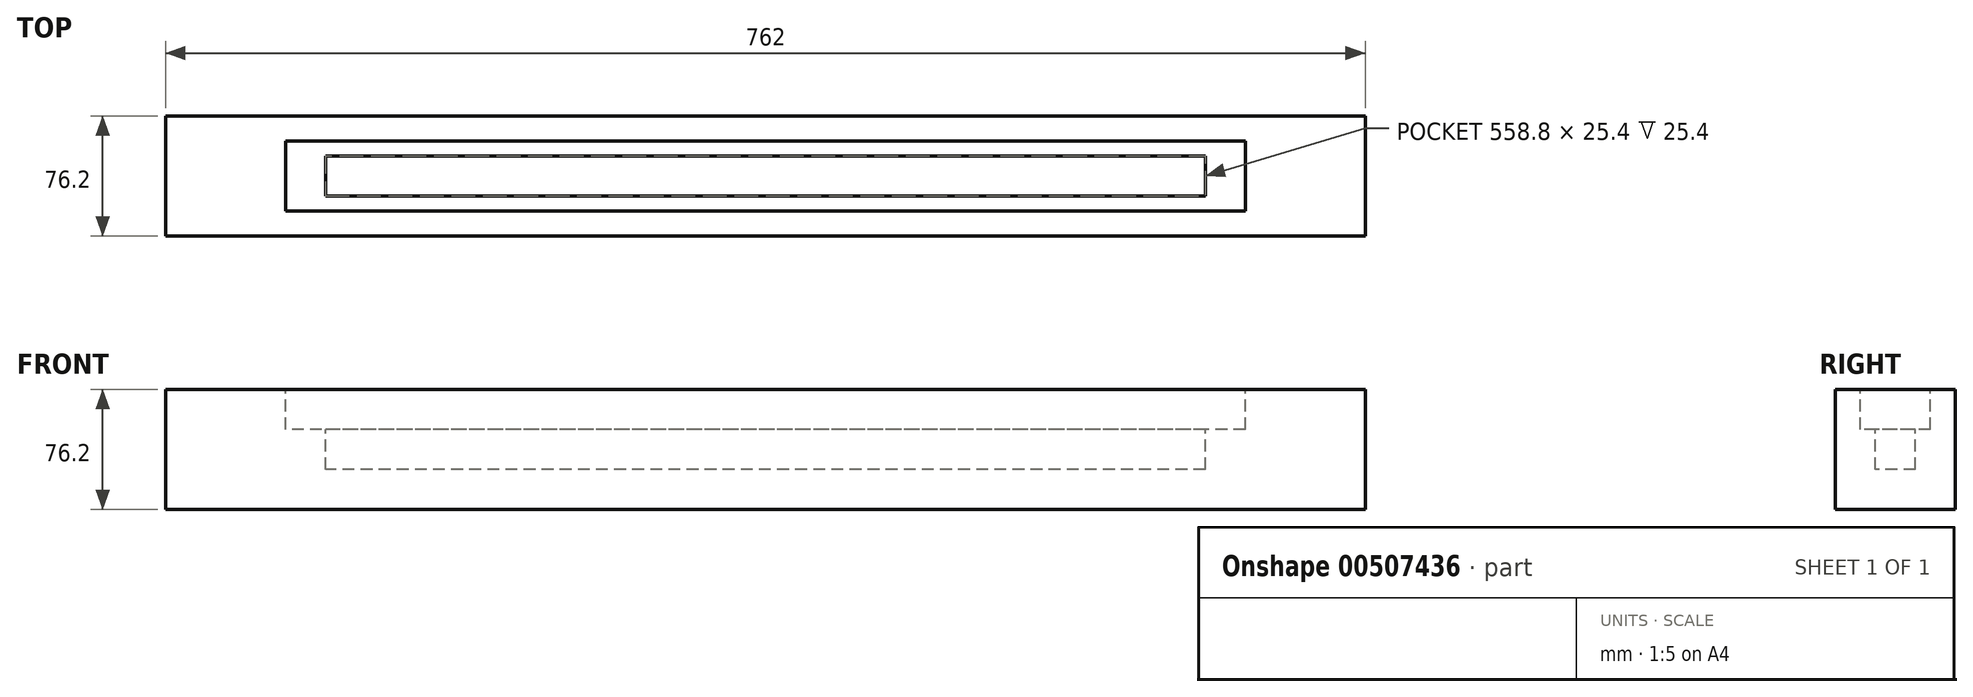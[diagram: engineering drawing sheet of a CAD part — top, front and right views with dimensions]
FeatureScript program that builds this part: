
annotation { "Feature Type Name" : "Feature", "Feature Type Description" : "" }
export const myFeature = defineFeature(function(context is Context, id is Id, definition is map)
    precondition{}
    {
        {
            var Q0;
            Q0=qCreatedBy(makeId("Front.planeOp"),FACE);
            var sketch = newSketch(context, id + "F0", { "sketchPlane" : qUnion([Q0])});
            skLineSegment(sketch, "E0.bottom", {"start": v(381, 38.1) * mm, "end": v(-381, 38.1) * mm});
            skLineSegment(sketch, "E0.top", {"start": v(381, -38.1) * mm, "end": v(-381, -38.1) * mm});
            skLineSegment(sketch, "E0.left", {"start": v(381, 38.1) * mm, "end": v(381, -38.1) * mm});
            skLineSegment(sketch, "E0.right", {"start": v(-381, 38.1) * mm, "end": v(-381, -38.1) * mm});
            skPoint(sketch, "E0.middle", {"position": v(0, 0) * mm});
            skSolve(sketch);
        }
        {
            var Q0;
            Q0 = qSketchRegion(id + "F0", true);
            extrude(context, id + "F1", {"entities" : qUnion([Q0]), "depth" : 76.2 * mm});
        }
        {
            var Q0;
            Q0=makeQuery(id+"F1.opExtrude","SWEPT_FACE",FACE,{"disambiguationData":[OSD([sQuery(id+"F0.wireOp",EDGE,"E0.bottom")])]});
            var sketch = newSketch(context, id + "F2", { "sketchPlane" : qUnion([Q0])});
            skLineSegment(sketch, "E1.bottom", {"start": v(304.8, -15.87) * mm, "end": v(-304.8, -15.88) * mm});
            skLineSegment(sketch, "E1.top", {"start": v(304.8, -60.32) * mm, "end": v(-304.8, -60.33) * mm});
            skLineSegment(sketch, "E1.left", {"start": v(304.8, -15.87) * mm, "end": v(304.8, -60.32) * mm});
            skLineSegment(sketch, "E1.right", {"start": v(-304.8, -15.88) * mm, "end": v(-304.8, -60.33) * mm});
            skPoint(sketch, "E1.middle", {"position": v(0, -38.1) * mm});
            skSolve(sketch);
        }
        {
            var Q0;
            Q0=makeQuery(id+"F2.imprint","IMPRINT",FACE,{"disambiguationData":[TD([[makeQuery(id+"F2.imprint","IMPRINT",EDGE,{"derivedFrom":sQuery(id+"F2.wireOp",EDGE,"E1.bottom")}),1.0]])]});
            extrude(context, id + "F3", {"entities" : qUnion([Q0]), "operationType" : NewBodyOperationType.REMOVE, "oppositeDirection" : true, "depth" : 25.4 * mm});
        }
        {
            var Q0;
            Q0=makeQuery(id+"F3.boolean.opBoolean","COPY",FACE,{"derivedFrom":makeQuery(id+"F3.opExtrude","CAP_FACE",FACE,{"disambiguationData":[OSD([sQuery(id+"F2.wireOp",EDGE,"E1.bottom"),sQuery(id+"F2.wireOp",EDGE,"E1.top"),sQuery(id+"F2.wireOp",EDGE,"E1.left"),sQuery(id+"F2.wireOp",EDGE,"E1.right")])],"isStart":false})});
            var sketch = newSketch(context, id + "F4", { "sketchPlane" : qUnion([Q0])});
            skLineSegment(sketch, "E2.bottom", {"start": v(279.4, -25.4) * mm, "end": v(-279.4, -25.4) * mm});
            skLineSegment(sketch, "E2.top", {"start": v(279.4, -50.8) * mm, "end": v(-279.4, -50.8) * mm});
            skLineSegment(sketch, "E2.left", {"start": v(279.4, -25.4) * mm, "end": v(279.4, -50.8) * mm});
            skLineSegment(sketch, "E2.right", {"start": v(-279.4, -25.4) * mm, "end": v(-279.4, -50.8) * mm});
            skPoint(sketch, "E2.middle", {"position": v(0, -38.1) * mm});
            skSolve(sketch);
        }
        {
            var Q0;
            Q0 = qSketchRegion(id + "F4", true);
            extrude(context, id + "F5", {"entities" : qUnion([Q0]), "operationType" : NewBodyOperationType.REMOVE, "oppositeDirection" : true, "depth" : 25.4 * mm});
        }
    });
